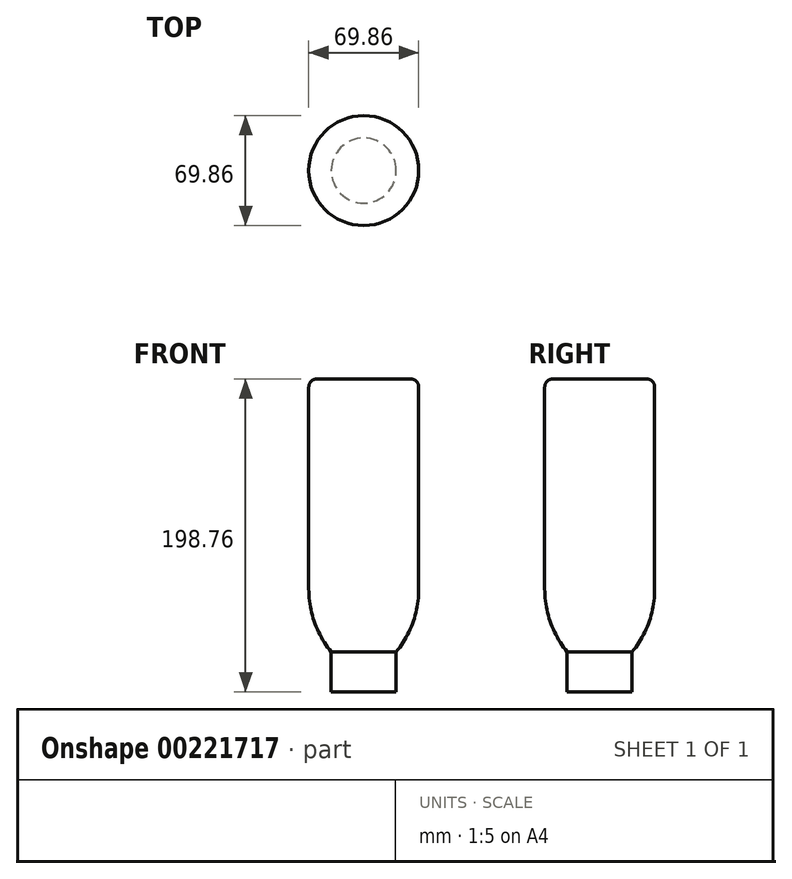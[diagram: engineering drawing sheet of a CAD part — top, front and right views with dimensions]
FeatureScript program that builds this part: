
annotation { "Feature Type Name" : "Feature", "Feature Type Description" : "" }
export const myFeature = defineFeature(function(context is Context, id is Id, definition is map)
    precondition{}
    {
        {
            var Q0;
            Q0=qCreatedBy(makeId("Front.planeOp"),FACE);
            var sketch = newSketch(context, id + "F0", { "sketchPlane" : qUnion([Q0])});
            skLineSegment(sketch, "E0", {"start": v(0, 173.36) * mm, "end": v(-34.93, 173.36) * mm});
            skLineSegment(sketch, "E1", {"start": v(-34.93, 173.36) * mm, "end": v(-34.92, 40) * mm});
            skLineSegment(sketch, "E2", {"start": v(-20.64, 0) * mm, "end": v(-20.64, -25.4) * mm});
            skLineSegment(sketch, "E3", {"start": v(-20.64, -25.4) * mm, "end": v(0, -25.4) * mm});
            skLineSegment(sketch, "E4", {"start": v(0, -25.4) * mm, "end": v(0, 173.36) * mm});
            skArc(sketch, "E5", {"start": v(-34.92, 40) * mm, "mid": v(-31.25, 18.77) * mm, "end": v(-20.64, 0) * mm});
            skSolve(sketch);
        }
        {
            var Q0;
            Q0=makeQuery(id+"F0.imprint","IMPRINT",FACE,{"disambiguationData":[TD([[makeQuery(id+"F0.imprint","IMPRINT",EDGE,{"derivedFrom":sQuery(id+"F0.wireOp",EDGE,"E0")}),1.0]])]});
            var Q1;
            Q1=sQuery(id+"F0.wireOp",EDGE,"E4");
            revolve(context, id + "F1", {"entities" : qUnion([Q0]), "axis" : qUnion([Q1]), "revolveType" : RevolveType.FULL});
        }
        {
            var Q0;
            Q0=makeQuery(id+"F1.opRevolve","SWEPT_EDGE",EDGE,{"disambiguationData":[OSD([sQuery(id+"F0.wireOp",EDGE,"E0"),sQuery(id+"F0.wireOp",EDGE,"E1")])]});
            fillet(context, id + "F2", {"entities" : qUnion([Q0]), "radius" : 5.08 * mm, "tangentPropagation" : true, "allowEdgeOverflow" : false});
        }
    });
